# Revit family: ACO AUS Gully 218 Telescopic - Square Top - Vertical Outlet with Location Flange - 300x3005
name_source: partatom
category: Plumbing Fixtures
revit_build: Autodesk Revit 2014 (Build: 20130308_1515(x64)
units: mm (PartAtom-declared; Revit-internal decimal feet)

## types (4) — shared parameters
160 mm Dia Outlet = Yes
Fax = +61 (2) 4747 4029
Gully Colour = passivated stainless steel surface ( matt grey)
Gully Outlet Radius = 80 mm  [stored 0.262467 ft]
Gully Recyclable = Fully recyclable
Fully recyclable
Gully Recycled Material Content = 20 - 30 %
Gully Top Size (mm) = To suit 300x300 grates
Load Class = A15 - C250 (EN 1253) and D210 (AS 3996)
Manufacturer = ACO Polycrete
Outlet Diameter (mm) = 160
Price = POA - contact ACO
Product Range = ACO Gully 218
Product Type = Point Drainage
Telephone = +61 (2) 4747 4000
Water Mark 1 = This file is the property of ACO Passavant
Water Mark 2 = This file is water marked and users are prohibited to reproduce, adapt, distribute this information
Water Marked With = BIM Manager Premium Suite
Website = www.acoaus.com.au

## per-type parameters (varying)
- 141994 - Adjustable Height with FAT SS 304: Flow Rate (l/s)=5-5.5; Foul Air Trap  &  Foul Air Trap Support Ring=Yes; Foul Air Trap Seal Colour=Black; Foul Air Trap Seal Material=NBR; Foul Air Trap Seal Recyclable=Fully recyclable; Foul Air Trap Seal Recycled Material Content=0%; Grating Product Code 408034=Load Class L15 (EN 1253) - Mesh grate - Slip Resistant - Stainless steel grade 304 - 268x268x25 - 2.1kg; Grating Product Code 408035=Load Class L15 (EN 1253) - Mesh grate - Plain - Stainless steel grade 304 - 268x268x25 - 2.1kg; Grating Product Code 408037=Load Class M125 (EN 1253) - Ladder grate - Slip Resistant - Stainless steel grade 304 - 168x168x25 - 4.3kg; Grating Product Code 408041=Load Class L15 (EN 1253) - Arla grate - Slip Resistant - Stainless steel grade 304 - 268x268x25 - 1.8kg; Grating Product Code 408045=Load Class D210 (EN 1253) - Ladder grate - Plain - Stainless steel grade 304 - 268x268x25 - 6.2kg; Grating product Code 142010=Load Class L15 (EN 1253) - 5 Star grate - Slip Resistant - Stainless steel grade 304 - 268x268x25 - 4.1kg; Grating product Code 416916=Load Class R50 (EN 1253) - Ladder grate - Slip Resistant - Stainless steel grade 304 - 268x268x25 - 3.5kg; Grating product Code 416944=Load Class M125 (EN 1253) - Cast grate - Slip Resistant - Stainless steel grade 304 - 168x168x25 - 5.6kg; Gully Material=Stainless Steel Grade 304; Gully Outlet Depth=74 mm  [stored 0.242782 ft]; Gully Product Code=141994; Gully Product Description=ACO Gully 218 adjustable height DN160 vertical outlet with square top section with Foul Air Trap - grade 304; Gully Weight (Kg)=5.8; Material=Stainless Steel AISI 304; Product Code 408223=0.7 litre removable strainer - Stainless steel grade 304 - 0.6kg; Product Code 408226=Waterproof bonding flange - Stainless steel grade 304 - 2.5kg; Product Code 413028=2.0 litre removable strainer - Stainless steel grade 304 - 0.9kg
- 141995 - Adjustable Height with FAT SS 316: Flow Rate (l/s)=5-5.5; Foul Air Trap  &  Foul Air Trap Support Ring=Yes; Foul Air Trap Seal Colour=Black; Foul Air Trap Seal Material=NBR; Foul Air Trap Seal Recyclable=Fully recyclable; Foul Air Trap Seal Recycled Material Content=0%; Grating Product Code 408134=Load Class L15 (EN 1253) - Mesh grate - Slip Resistant - Stainless steel grade 316 - 268x268x25 - 2.1kg; Grating Product Code 408135=Load Class L15 (EN 1253) - Mesh grate - Plain - Stainless steel grade 316 - 268x268x25 - 2.1kg; Grating Product Code 408141=Load Class L15 (EN 1253) - Arla grate - Slip Resistant - Stainless steel grade 316 - 268x268x25 - 1.8kg; Grating product Code 408137=Load Class M125 (EN 1253) - Ladder grate - Slip Resistant - Stainless steel grade 316 - 268x268x25 - 4.3kg; Grating product Code 408145=Load Class D210 (EN 1253) - Ladder grate - Plain - Stainless steel grade 316 - 268x268x25 - 6.2kg; Grating product Code 416917=Load Class R50 (EN 1253) - Ladder grate - Slip Resistant - Stainless steel grade 316 - 268x268x25 - 3.5kg; Gully Material=Stainless Steel Grade 316; Gully Outlet Depth=77 mm; Gully Product Code=141995; Gully Product Description=ACO Gully 218 adjustable height DN160 vertical outlet with square top section with Foul Air Trap - grade 316; Gully Weight (Kg)=5.8; Material=Stainless Steel AISI 316; Product Code 142002=Retention chain connecting fixed strainer to FAT - Stainless steel grade 316 - 0.1kg; Product Code 142003=Retention chain connecting fixed strainer to removable strainer - Stainless steel grade 316 - 0.1kg; Product Code 142004=Retention chain connecting to FAT to removable strainer - Stainless steel grade 316 - 0.1kg; Product Code 142005=Retention chain connecting removable strainer to grate - Stainless steel grade 316 - 0.1kg; Product Code 142006=Retention chain connecting removable FAT to grate - Stainless steel grade 316 - 0.1kg; Product Code 142008=Fixed strainer to suit a 160mm outlet - Stainless steel grade 316 - 0.1kg; Product Code 408233=0.7 litre removable strainer - Stainless steel grade 316 - 0.6kg; Product Code 408236=Waterproof bonding flange - Stainless steel grade 316 - 2.5kg; Product Code 413029=2.0 litre removable strainer - Stainless steel grade 316 - 0.9kg
- 141992 - Adjustable Height without FAT SS 304: Flow Rate (l/s)=27.1; Foul Air Trap  &  Foul Air Trap Support Ring=No; Grating Product Code 408034=Load Class L15 (EN 1253) - Mesh grate - Slip Resistant - Stainless steel grade 304 - 268x268x25 - 2.1kg; Grating Product Code 408035=Load Class L15 (EN 1253) - Mesh grate - Plain - Stainless steel grade 304 - 268x268x25 - 2.1kg; Grating Product Code 408037=Load Class M125 (EN 1253) - Ladder grate - Slip Resistant - Stainless steel grade 304 - 168x168x25 - 4.3kg; Grating Product Code 408041=Load Class L15 (EN 1253) - Arla grate - Slip Resistant - Stainless steel grade 304 - 268x268x25 - 1.8kg; Grating Product Code 408045=Load Class D210 (EN 1253) - Ladder grate - Plain - Stainless steel grade 304 - 268x268x25 - 6.2kg; Grating product Code 142010=Load Class L15 (EN 1253) - 5 Star grate - Slip Resistant - Stainless steel grade 304 - 268x268x25 - 4.1kg; Grating product Code 416916=Load Class R50 (EN 1253) - Ladder grate - Slip Resistant - Stainless steel grade 304 - 268x268x25 - 3.5kg; Grating product Code 416944=Load Class M125 (EN 1253) - Cast grate - Slip Resistant - Stainless steel grade 304 - 168x168x25 - 5.6kg; Gully Material=Stainless Steel Grade 304; Gully Outlet Depth=74 mm  [stored 0.242782 ft]; Gully Product Code=141992; Gully Product Description=ACO Gully 218 adjustable height DN160 vertical outlet with square top section without Foul Air Trap - grade 304; Gully Weight (Kg)=4.8; Material=Stainless Steel AISI 304; Product Code 408223=0.7 litre removable strainer - Stainless steel grade 304 - 0.6kg; Product Code 408226=Waterproof bonding flange - Stainless steel grade 304 - 2.5kg; Product Code 413028=2.0 litre removable strainer - Stainless steel grade 304 - 0.9kg
- 141993 - Adjustable Height without FAT SS 316: Flow Rate (l/s)=27.1; Foul Air Trap  &  Foul Air Trap Support Ring=No; Grating Product Code 408134=Load Class L15 (EN 1253) - Mesh grate - Slip Resistant - Stainless steel grade 316 - 268x268x25 - 2.1kg; Grating Product Code 408135=Load Class L15 (EN 1253) - Mesh grate - Plain - Stainless steel grade 316 - 268x268x25 - 2.1kg; Grating Product Code 408141=Load Class L15 (EN 1253) - Arla grate - Slip Resistant - Stainless steel grade 316 - 268x268x25 - 1.8kg; Grating product Code 408137=Load Class M125 (EN 1253) - Ladder grate - Slip Resistant - Stainless steel grade 316 - 268x268x25 - 4.3kg; Grating product Code 408145=Load Class D210 (EN 1253) - Ladder grate - Plain - Stainless steel grade 316 - 268x268x25 - 6.2kg; Grating product Code 416917=Load Class R50 (EN 1253) - Ladder grate - Slip Resistant - Stainless steel grade 316 - 268x268x25 - 3.5kg; Gully Material=Stainless Steel Grade 316; Gully Outlet Depth=74 mm  [stored 0.242782 ft]; Gully Product Code=141993; Gully Product Description=ACO Gully 218 adjustable height DN160 vertical outlet with square top section without Foul Air Trap - grade 316; Gully Weight (Kg)=4.8; Material=Stainless Steel AISI 316; Product Code 142003=Retention chain connecting fixed strainer to removable strainer - Stainless steel grade 316 - 0.1kg; Product Code 142005=Retention chain connecting removable strainer to grate - Stainless steel grade 316 - 0.1kg; Product Code 142008=Fixed strainer to suit a 160mm outlet - Stainless steel grade 316 - 0.1kg; Product Code 408233=0.7 litre removable strainer - Stainless steel grade 316 - 0.6kg; Product Code 408236=Waterproof bonding flange - Stainless steel grade 316 - 2.5kg; Product Code 413029=2.0 litre removable strainer - Stainless steel grade 316 - 0.9kg

note: [stored X ft] marks values corroborated as IEEE doubles in the binary element streams (Revit-internal decimal feet)

## geometry (parser evidence)
native form markers: Blend x2, Sweep x6
no freeform markers — native parametric forms only
